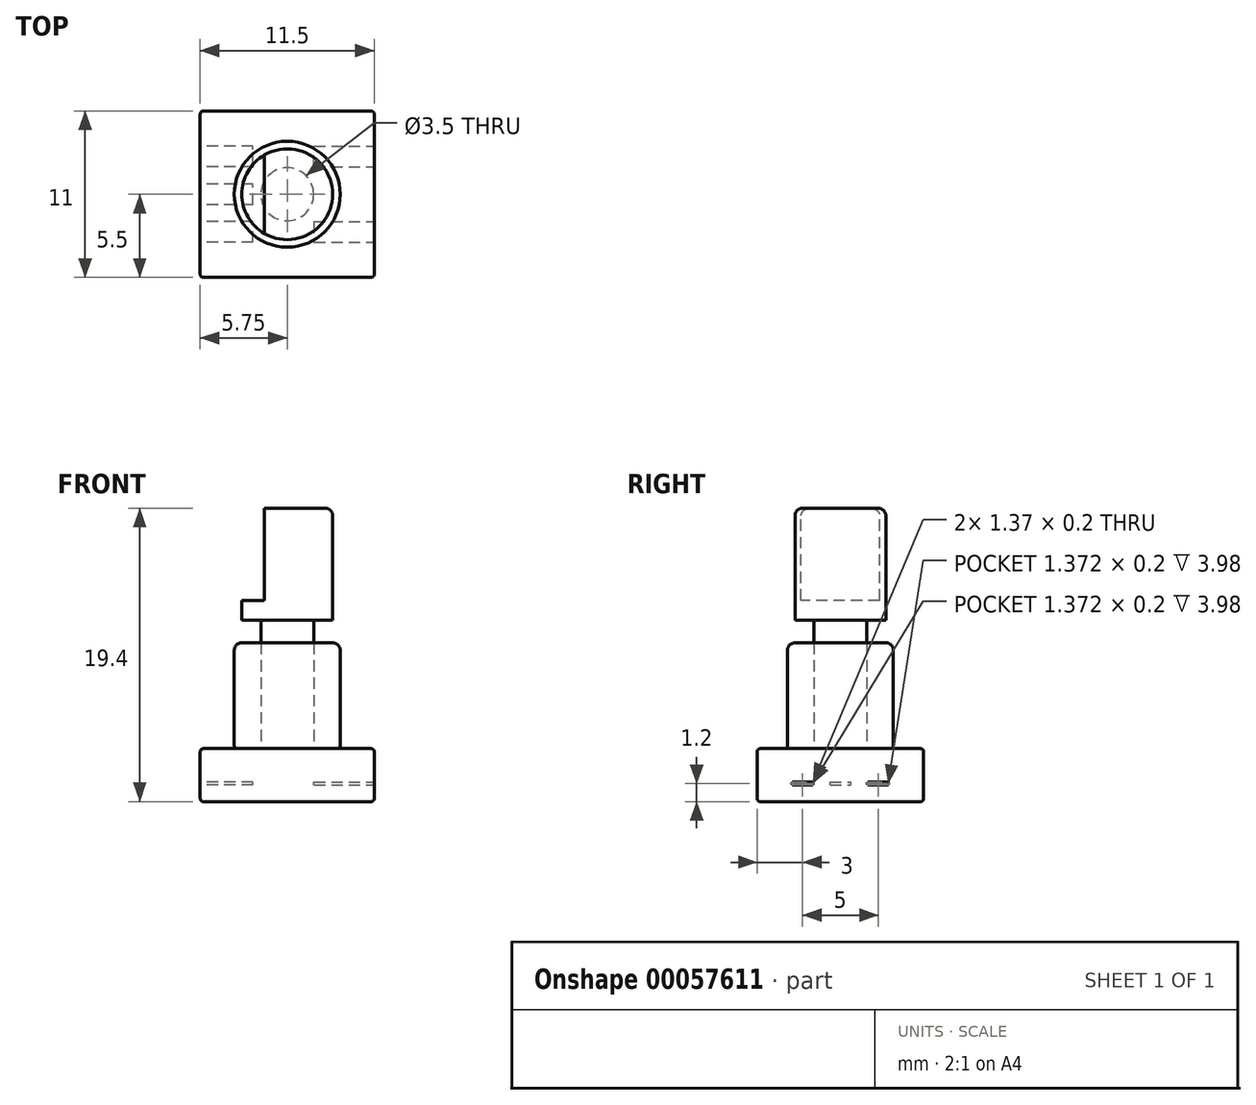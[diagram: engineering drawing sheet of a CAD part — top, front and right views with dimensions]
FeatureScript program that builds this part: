
annotation { "Feature Type Name" : "Feature", "Feature Type Description" : "" }
export const myFeature = defineFeature(function(context is Context, id is Id, definition is map)
    precondition{}
    {
        {
            var Q0;
            Q0=qCreatedBy(makeId("Top.planeOp"),FACE);
            var sketch = newSketch(context, id + "F0", { "sketchPlane" : qUnion([Q0])});
            skLineSegment(sketch, "E0.bottom", {"start": v(5.75, -5.5) * mm, "end": v(-5.75, -5.5) * mm});
            skLineSegment(sketch, "E0.top", {"start": v(5.75, 5.5) * mm, "end": v(-5.75, 5.5) * mm});
            skLineSegment(sketch, "E0.left", {"start": v(5.75, -5.5) * mm, "end": v(5.75, 5.5) * mm});
            skLineSegment(sketch, "E0.right", {"start": v(-5.75, -5.5) * mm, "end": v(-5.75, 5.5) * mm});
            skPoint(sketch, "E0.middle", {"position": v(0, 0) * mm});
            skSolve(sketch);
        }
        {
            var Q0;
            Q0=makeQuery(id+"F0.imprint","IMPRINT",FACE,{"disambiguationData":[TD([[makeQuery(id+"F0.imprint","IMPRINT",EDGE,{"derivedFrom":sQuery(id+"F0.wireOp",EDGE,"E0.bottom")}),-1.0]])]});
            extrude(context, id + "F1", {"entities" : qUnion([Q0]), "oppositeDirection" : true, "depth" : 3.5 * mm});
        }
        {
            var Q0;
            Q0=makeQuery(id+"F1.opExtrude","CAP_FACE",FACE,{"disambiguationData":[OSD([sQuery(id+"F0.wireOp",EDGE,"E0.bottom"),sQuery(id+"F0.wireOp",EDGE,"E0.top"),sQuery(id+"F0.wireOp",EDGE,"E0.left"),sQuery(id+"F0.wireOp",EDGE,"E0.right")])],"isStart":true});
            var sketch = newSketch(context, id + "F2", { "sketchPlane" : qUnion([Q0])});
            skCircle(sketch, "E1", {"center": v(0, 0) * mm, "radius": 3.5 * mm});
            skCircle(sketch, "E2", {"center": v(0, 0) * mm, "radius": 1.75 * mm});
            skSolve(sketch);
        }
        {
            var Q0;
            Q0=makeQuery(id+"F2.imprint","IMPRINT",FACE,{"disambiguationData":[TD([[makeQuery(id+"F2.imprint","IMPRINT",EDGE,{"derivedFrom":sQuery(id+"F2.wireOp",EDGE,"E1")}),1.0]])]});
            extrude(context, id + "F3", {"entities" : qUnion([Q0]), "depth" : 7 * mm});
        }
        {
            var Q0;
            Q0=makeQuery(id+"F2.imprint","IMPRINT",FACE,{"disambiguationData":[TD([[makeQuery(id+"F2.imprint","IMPRINT",EDGE,{"derivedFrom":sQuery(id+"F2.wireOp",EDGE,"E2")}),1.0]])]});
            extrude(context, id + "F4", {"entities" : qUnion([Q0]), "depth" : 8.5 * mm});
        }
        {
            var Q0;
            Q0=makeQuery(id+"F4.opExtrude","CAP_FACE",FACE,{"disambiguationData":[OSD([sQuery(id+"F2.wireOp",EDGE,"E2")])],"isStart":false});
            var sketch = newSketch(context, id + "F5", { "sketchPlane" : qUnion([Q0])});
            skCircle(sketch, "E3", {"center": v(0, 0) * mm, "radius": 3 * mm});
            skSolve(sketch);
        }
        {
            var Q0;
            Q0=makeQuery(id+"F5.imprint","IMPRINT",FACE,{"disambiguationData":[TD([[makeQuery(id+"F5.imprint","IMPRINT",EDGE,{"derivedFrom":makeQuery(id+"F4.opExtrude","CAP_EDGE",EDGE,{"disambiguationData":[OSD([sQuery(id+"F2.wireOp",EDGE,"E2")])],"isStart":false})}),1.0]])]});
            var Q1;
            Q1=makeQuery(id+"F5.imprint","IMPRINT",FACE,{"disambiguationData":[TD([[makeQuery(id+"F5.imprint","IMPRINT",EDGE,{"derivedFrom":sQuery(id+"F5.wireOp",EDGE,"E3")}),1.0]])]});
            extrude(context, id + "F6", {"entities" : qUnion([Q0, Q1]), "operationType" : NewBodyOperationType.ADD, "depth" : 7.4 * mm});
        }
        {
            var Q0;
            Q0=makeQuery(id+"F6.opExtrude","CAP_FACE",FACE,{"disambiguationData":[OSD([sQuery(id+"F5.wireOp",EDGE,"E3")])],"isStart":false});
            var sketch = newSketch(context, id + "F7", { "sketchPlane" : qUnion([Q0])});
            skLineSegment(sketch, "E4", {"start": v(-1.5, 2.6) * mm, "end": v(-1.5, -2.6) * mm});
            skSolve(sketch);
        }
        {
            var Q0;
            {var subQ0=sQuery(id+"F7.wireOp",EDGE,"E4");Q0=makeQuery(id+"F7.imprint","IMPRINT",FACE,{"disambiguationData":[TD([[makeQuery(id+"F7.imprint","IMPRINT",EDGE,{"derivedFrom":subQ0}),-1.0]])]});}
            extrude(context, id + "F8", {"entities" : qUnion([Q0]), "operationType" : NewBodyOperationType.REMOVE, "oppositeDirection" : true, "depth" : 6 * mm});
        }
        {
            var Q0;
            Q0=makeQuery(id+"F1.opExtrude","CAP_EDGE",EDGE,{"disambiguationData":[OSD([sQuery(id+"F0.wireOp",EDGE,"E0.bottom")])],"isStart":true});
            var Q1;
            Q1=makeQuery(id+"F1.opExtrude","CAP_EDGE",EDGE,{"disambiguationData":[OSD([sQuery(id+"F0.wireOp",EDGE,"E0.right")])],"isStart":true});
            var Q2;
            Q2=makeQuery(id+"F1.opExtrude","CAP_EDGE",EDGE,{"disambiguationData":[OSD([sQuery(id+"F0.wireOp",EDGE,"E0.top")])],"isStart":true});
            var Q3;
            Q3=makeQuery(id+"F1.opExtrude","CAP_EDGE",EDGE,{"disambiguationData":[OSD([sQuery(id+"F0.wireOp",EDGE,"E0.left")])],"isStart":true});
            var Q4;
            Q4=makeQuery(id+"F1.opExtrude","SWEPT_EDGE",EDGE,{"disambiguationData":[OSD([sQuery(id+"F0.wireOp",EDGE,"E0.bottom"),sQuery(id+"F0.wireOp",EDGE,"E0.left")])]});
            var Q5;
            Q5=makeQuery(id+"F1.opExtrude","SWEPT_EDGE",EDGE,{"disambiguationData":[OSD([sQuery(id+"F0.wireOp",EDGE,"E0.bottom"),sQuery(id+"F0.wireOp",EDGE,"E0.right")])]});
            var Q6;
            Q6=makeQuery(id+"F1.opExtrude","CAP_EDGE",EDGE,{"disambiguationData":[OSD([sQuery(id+"F0.wireOp",EDGE,"E0.bottom")])],"isStart":false});
            var Q7;
            Q7=makeQuery(id+"F1.opExtrude","CAP_EDGE",EDGE,{"disambiguationData":[OSD([sQuery(id+"F0.wireOp",EDGE,"E0.right")])],"isStart":false});
            var Q8;
            Q8=makeQuery(id+"F1.opExtrude","CAP_EDGE",EDGE,{"disambiguationData":[OSD([sQuery(id+"F0.wireOp",EDGE,"E0.left")])],"isStart":false});
            var Q9;
            Q9=makeQuery(id+"F1.opExtrude","SWEPT_EDGE",EDGE,{"disambiguationData":[OSD([sQuery(id+"F0.wireOp",EDGE,"E0.top"),sQuery(id+"F0.wireOp",EDGE,"E0.left")])]});
            var Q10;
            Q10=makeQuery(id+"F1.opExtrude","SWEPT_EDGE",EDGE,{"disambiguationData":[OSD([sQuery(id+"F0.wireOp",EDGE,"E0.top"),sQuery(id+"F0.wireOp",EDGE,"E0.right")])]});
            var Q11;
            Q11=makeQuery(id+"F1.opExtrude","CAP_EDGE",EDGE,{"disambiguationData":[OSD([sQuery(id+"F0.wireOp",EDGE,"E0.top")])],"isStart":false});
            var Q12;
            Q12=makeQuery(id+"F3.opExtrude","CAP_EDGE",EDGE,{"disambiguationData":[OSD([sQuery(id+"F2.wireOp",EDGE,"E1")])],"isStart":true});
            fillet(context, id + "F9", {"entities" : qUnion([Q0, Q1, Q2, Q3, Q4, Q5, Q6, Q7, Q8, Q9, Q10, Q11, Q12]), "radius" : .2 * mm, "tangentPropagation" : true, "allowEdgeOverflow" : false});
        }
        {
            var Q0;
            Q0=makeQuery(id+"F6.opExtrude","CAP_EDGE",EDGE,{"disambiguationData":[OSD([sQuery(id+"F5.wireOp",EDGE,"E3")])],"isStart":false});
            var Q1;
            Q1=makeQuery(id+"F3.opExtrude","CAP_EDGE",EDGE,{"disambiguationData":[OSD([sQuery(id+"F2.wireOp",EDGE,"E1")])],"isStart":false});
            fillet(context, id + "F10", {"entities" : qUnion([Q0, Q1]), "radius" : .5 * mm, "tangentPropagation" : true, "allowEdgeOverflow" : false});
        }
        {
            var Q0;
            {var subQ0=sQuery(id+"F7.wireOp",EDGE,"E4");Q0=makeQuery(id+"F7.imprint","IMPRINT",FACE,{"disambiguationData":[TD([[makeQuery(id+"F7.imprint","IMPRINT",EDGE,{"derivedFrom":subQ0}),-1.0]])]});}
            extrude(context, id + "F11", {"entities" : qUnion([Q0]), "operationType" : NewBodyOperationType.REMOVE, "oppositeDirection" : true, "depth" : 6.1 * mm});
        }
        {
            var Q0;
            Q0=makeQuery(id+"F1.opExtrude","SWEPT_FACE",FACE,{"disambiguationData":[OSD([sQuery(id+"F0.wireOp",EDGE,"E0.right")])]});
            var sketch = newSketch(context, id + "F12", { "sketchPlane" : qUnion([Q0])});
            skLineSegment(sketch, "E5.bottom", {"start": v(-1.81, -2.4) * mm, "end": v(-3.19, -2.4) * mm});
            skLineSegment(sketch, "E5.top", {"start": v(-1.81, -2.2) * mm, "end": v(-3.19, -2.2) * mm});
            skLineSegment(sketch, "E5.left", {"start": v(-1.81, -2.4) * mm, "end": v(-1.81, -2.2) * mm});
            skLineSegment(sketch, "E5.right", {"start": v(-3.19, -2.4) * mm, "end": v(-3.19, -2.2) * mm});
            skPoint(sketch, "E5.middle", {"position": v(-2.5, -2.3) * mm});
            skLineSegment(sketch, "E6.1.0.0", {"start": v(0.69, -2.2) * mm, "end": v(-0.69, -2.2) * mm});
            skLineSegment(sketch, "E6.1.0.1", {"start": v(0.69, -2.4) * mm, "end": v(-0.69, -2.4) * mm});
            skLineSegment(sketch, "E6.1.0.2", {"start": v(0.69, -2.4) * mm, "end": v(0.69, -2.2) * mm});
            skLineSegment(sketch, "E6.1.0.3", {"start": v(-0.69, -2.4) * mm, "end": v(-0.69, -2.2) * mm});
            skLineSegment(sketch, "E6.2.0.0", {"start": v(3.19, -2.2) * mm, "end": v(1.81, -2.2) * mm});
            skLineSegment(sketch, "E6.2.0.1", {"start": v(3.19, -2.4) * mm, "end": v(1.81, -2.4) * mm});
            skLineSegment(sketch, "E6.2.0.2", {"start": v(3.19, -2.4) * mm, "end": v(3.19, -2.2) * mm});
            skLineSegment(sketch, "E6.2.0.3", {"start": v(1.81, -2.4) * mm, "end": v(1.81, -2.2) * mm});
            skLineSegment(sketch, "E6.direction1", {"start": v(-3.19, -2.2) * mm, "end": v(-0.69, -2.2) * mm, "construction": true});
            skSolve(sketch);
        }
        {
            var Q0;
            Q0=makeQuery(id+"F12.imprint","IMPRINT",FACE,{"disambiguationData":[TD([[makeQuery(id+"F12.imprint","IMPRINT",EDGE,{"derivedFrom":sQuery(id+"F12.wireOp",EDGE,"E5.bottom")}),-1.0]])]});
            var Q1;
            Q1=makeQuery(id+"F12.imprint","IMPRINT",FACE,{"disambiguationData":[TD([[makeQuery(id+"F12.imprint","IMPRINT",EDGE,{"derivedFrom":sQuery(id+"F12.wireOp",EDGE,"E6.1.0.0")}),1.0]])]});
            var Q2;
            Q2=makeQuery(id+"F12.imprint","IMPRINT",FACE,{"disambiguationData":[TD([[makeQuery(id+"F12.imprint","IMPRINT",EDGE,{"derivedFrom":sQuery(id+"F12.wireOp",EDGE,"E6.2.0.0")}),1.0]])]});
            extrude(context, id + "F13", {"entities" : qUnion([Q0, Q1, Q2]), "operationType" : NewBodyOperationType.REMOVE, "oppositeDirection" : true, "depth" : 3.48 * mm});
        }
        {
            var Q0;
            Q0=makeQuery(id+"F1.opExtrude","SWEPT_FACE",FACE,{"disambiguationData":[OSD([sQuery(id+"F0.wireOp",EDGE,"E0.left")])]});
            var sketch = newSketch(context, id + "F14", { "sketchPlane" : qUnion([Q0])});
            skLineSegment(sketch, "E7.bottom", {"start": v(-1.81, -2.4) * mm, "end": v(-3.19, -2.4) * mm});
            skLineSegment(sketch, "E7.top", {"start": v(-1.81, -2.2) * mm, "end": v(-3.19, -2.2) * mm});
            skLineSegment(sketch, "E7.left", {"start": v(-1.81, -2.4) * mm, "end": v(-1.81, -2.2) * mm});
            skLineSegment(sketch, "E7.right", {"start": v(-3.19, -2.4) * mm, "end": v(-3.19, -2.2) * mm});
            skPoint(sketch, "E7.middle", {"position": v(-2.5, -2.3) * mm});
            skLineSegment(sketch, "E8.MirrorCS", {"start": v(1.81, -2.2) * mm, "end": v(3.19, -2.2) * mm});
            skLineSegment(sketch, "E9.MirrorCS", {"start": v(1.81, -2.4) * mm, "end": v(3.19, -2.4) * mm});
            skLineSegment(sketch, "E10.MirrorCS", {"start": v(3.19, -2.4) * mm, "end": v(3.19, -2.2) * mm});
            skLineSegment(sketch, "E11.MirrorCS", {"start": v(1.81, -2.4) * mm, "end": v(1.81, -2.2) * mm});
            skSolve(sketch);
        }
        {
            var Q0;
            Q0=makeQuery(id+"F14.imprint","IMPRINT",FACE,{"disambiguationData":[TD([[makeQuery(id+"F14.imprint","IMPRINT",EDGE,{"derivedFrom":sQuery(id+"F14.wireOp",EDGE,"E7.bottom")}),-1.0]])]});
            var Q1;
            Q1=makeQuery(id+"F14.imprint","IMPRINT",FACE,{"disambiguationData":[TD([[makeQuery(id+"F14.imprint","IMPRINT",EDGE,{"derivedFrom":sQuery(id+"F14.wireOp",EDGE,"E8.MirrorCS")}),-1.0]])]});
            extrude(context, id + "F15", {"entities" : qUnion([Q0, Q1]), "operationType" : NewBodyOperationType.REMOVE, "oppositeDirection" : true, "depth" : 3.98 * mm});
        }
    });
